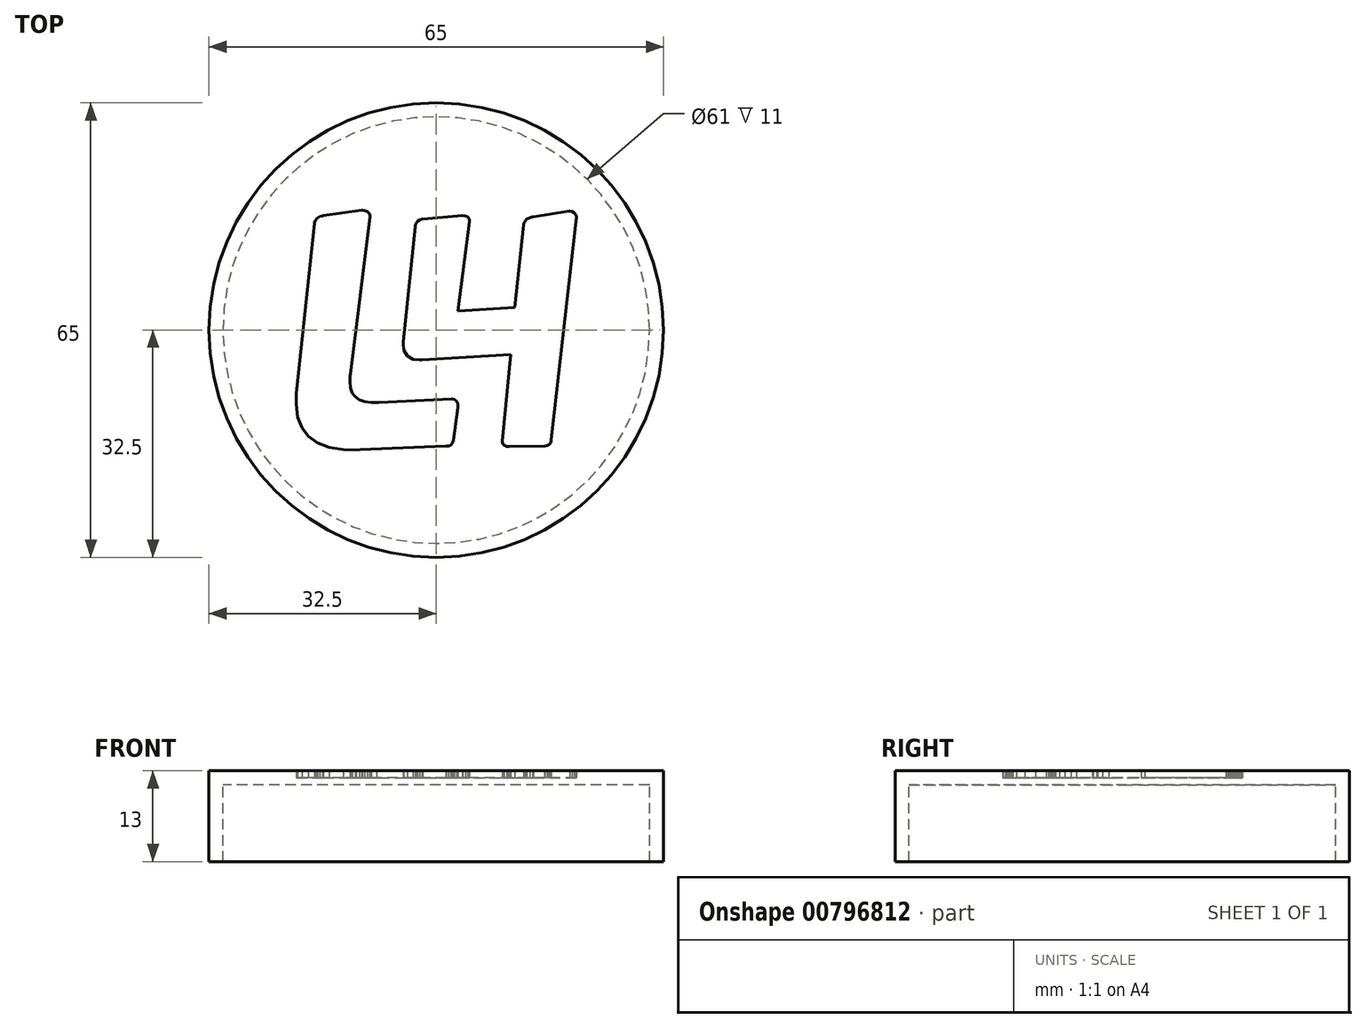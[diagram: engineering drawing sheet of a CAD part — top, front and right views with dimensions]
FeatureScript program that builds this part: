
annotation { "Feature Type Name" : "Feature", "Feature Type Description" : "" }
export const myFeature = defineFeature(function(context is Context, id is Id, definition is map)
    precondition{}
    {
        {
            var Q0;
            Q0=qCreatedBy(makeId("Top.planeOp"),FACE);
            var sketch = newSketch(context, id + "F0", { "sketchPlane" : qUnion([Q0])});
            skCircle(sketch, "E0", {"center": v(0, 0) * mm, "radius": 32.5 * mm});
            skSolve(sketch);
        }
        {
            var Q0;
            Q0 = qSketchRegion(id + "F0", true);
            extrude(context, id + "F1", {"entities" : qUnion([Q0]), "depth" : 2 * mm, "offsetDistance" : 25 * mm});
        }
        {
            var Q0;
            Q0=qCreatedBy(makeId("Top.planeOp"),FACE);
            var sketch = newSketch(context, id + "F2", { "sketchPlane" : qUnion([Q0])});
            skCircle(sketch, "E1.0", {"center": v(0, 0) * mm, "radius": 32.5 * mm});
            skCircle(sketch, "E2", {"center": v(0, 0) * mm, "radius": 30.5 * mm});
            skSolve(sketch);
        }
        {
            var Q0;
            Q0 = qSketchRegion(id + "F2", true);
            extrude(context, id + "F3", {"entities" : qUnion([Q0]), "operationType" : NewBodyOperationType.ADD, "oppositeDirection" : true, "depth" : 11 * mm, "offsetDistance" : 25 * mm});
        }
        {
            var Q0;
            Q0=qCreatedBy(makeId("Top.planeOp"),FACE);
            var sketch = newSketch(context, id + "F4", { "sketchPlane" : qUnion([Q0])});
            skLineSegment(sketch, "E3", {"start": v(2.44, -15.74) * mm, "end": v(2.42, -15.85) * mm});
            skLineSegment(sketch, "E4", {"start": v(2.42, -15.85) * mm, "end": v(2.32, -16.15) * mm});
            skLineSegment(sketch, "E5", {"start": v(2.32, -16.15) * mm, "end": v(2.1, -16.42) * mm});
            skLineSegment(sketch, "E6", {"start": v(2.1, -16.42) * mm, "end": v(1.79, -16.56) * mm});
            skLineSegment(sketch, "E7", {"start": v(1.79, -16.56) * mm, "end": v(1.48, -16.6) * mm});
            skLineSegment(sketch, "E8", {"start": v(1.48, -16.6) * mm, "end": v(1.38, -16.6) * mm});
            skLineSegment(sketch, "E9", {"start": v(1.38, -16.6) * mm, "end": v(-10.86, -17.1) * mm});
            skLineSegment(sketch, "E10", {"start": v(-10.86, -17.1) * mm, "end": v(-11.46, -17.13) * mm});
            skLineSegment(sketch, "E11", {"start": v(-11.46, -17.13) * mm, "end": v(-13.3, -17.07) * mm});
            skLineSegment(sketch, "E12", {"start": v(-13.3, -17.07) * mm, "end": v(-15.33, -16.74) * mm});
            skLineSegment(sketch, "E13", {"start": v(-15.33, -16.74) * mm, "end": v(-17, -16.1) * mm});
            skLineSegment(sketch, "E14", {"start": v(-17, -16.1) * mm, "end": v(-18.29, -15.17) * mm});
            skLineSegment(sketch, "E15", {"start": v(-18.29, -15.17) * mm, "end": v(-19.22, -13.94) * mm});
            skLineSegment(sketch, "E16", {"start": v(-19.22, -13.94) * mm, "end": v(-19.8, -12.42) * mm});
            skLineSegment(sketch, "E17", {"start": v(-19.8, -12.42) * mm, "end": v(-20.04, -10.59) * mm});
            skLineSegment(sketch, "E18", {"start": v(-20.04, -10.59) * mm, "end": v(-20.01, -9) * mm});
            skLineSegment(sketch, "E19", {"start": v(-20.01, -9) * mm, "end": v(-19.96, -8.46) * mm});
            skLineSegment(sketch, "E20", {"start": v(-19.96, -8.46) * mm, "end": v(-17.43, 15.25) * mm});
            skLineSegment(sketch, "E21", {"start": v(-17.43, 15.25) * mm, "end": v(-17.42, 15.35) * mm});
            skLineSegment(sketch, "E22", {"start": v(-17.42, 15.35) * mm, "end": v(-17.3, 15.66) * mm});
            skLineSegment(sketch, "E23", {"start": v(-17.3, 15.66) * mm, "end": v(-17.02, 16) * mm});
            skLineSegment(sketch, "E24", {"start": v(-17.02, 16) * mm, "end": v(-16.63, 16.23) * mm});
            skLineSegment(sketch, "E25", {"start": v(-16.63, 16.23) * mm, "end": v(-16.28, 16.34) * mm});
            skLineSegment(sketch, "E26", {"start": v(-16.28, 16.34) * mm, "end": v(-16.16, 16.36) * mm});
            skLineSegment(sketch, "E27", {"start": v(-16.16, 16.36) * mm, "end": v(-10.65, 17.12) * mm});
            skLineSegment(sketch, "E28", {"start": v(-10.65, 17.12) * mm, "end": v(-10.55, 17.13) * mm});
            skLineSegment(sketch, "E29", {"start": v(-10.55, 17.13) * mm, "end": v(-10.2, 17.1) * mm});
            skLineSegment(sketch, "E30", {"start": v(-10.2, 17.1) * mm, "end": v(-9.83, 16.93) * mm});
            skLineSegment(sketch, "E31", {"start": v(-9.83, 16.93) * mm, "end": v(-9.57, 16.62) * mm});
            skLineSegment(sketch, "E32", {"start": v(-9.57, 16.62) * mm, "end": v(-9.48, 16.3) * mm});
            skLineSegment(sketch, "E33", {"start": v(-9.48, 16.3) * mm, "end": v(-9.5, 16.2) * mm});
            skLineSegment(sketch, "E34", {"start": v(-9.5, 16.2) * mm, "end": v(-12.27, -6.3) * mm});
            skLineSegment(sketch, "E35", {"start": v(-12.27, -6.3) * mm, "end": v(-12.3, -6.56) * mm});
            skLineSegment(sketch, "E36", {"start": v(-12.3, -6.56) * mm, "end": v(-12.34, -7.37) * mm});
            skLineSegment(sketch, "E37", {"start": v(-12.34, -7.37) * mm, "end": v(-12.24, -8.27) * mm});
            skLineSegment(sketch, "E38", {"start": v(-12.24, -8.27) * mm, "end": v(-11.98, -8.99) * mm});
            skLineSegment(sketch, "E39", {"start": v(-11.98, -8.99) * mm, "end": v(-11.56, -9.54) * mm});
            skLineSegment(sketch, "E40", {"start": v(-11.56, -9.54) * mm, "end": v(-10.97, -9.95) * mm});
            skLineSegment(sketch, "E41", {"start": v(-10.97, -9.95) * mm, "end": v(-10.22, -10.2) * mm});
            skLineSegment(sketch, "E42", {"start": v(-10.22, -10.2) * mm, "end": v(-9.3, -10.33) * mm});
            skLineSegment(sketch, "E43", {"start": v(-9.3, -10.33) * mm, "end": v(-8.5, -10.35) * mm});
            skLineSegment(sketch, "E44", {"start": v(-8.5, -10.35) * mm, "end": v(-8.23, -10.33) * mm});
            skLineSegment(sketch, "E45", {"start": v(-8.23, -10.33) * mm, "end": v(2.19, -9.83) * mm});
            skLineSegment(sketch, "E46", {"start": v(2.19, -9.83) * mm, "end": v(2.3, -9.82) * mm});
            skLineSegment(sketch, "E47", {"start": v(2.3, -9.82) * mm, "end": v(2.62, -9.9) * mm});
            skLineSegment(sketch, "E48", {"start": v(2.62, -9.9) * mm, "end": v(2.93, -10.15) * mm});
            skLineSegment(sketch, "E49", {"start": v(2.93, -10.15) * mm, "end": v(3.09, -10.55) * mm});
            skLineSegment(sketch, "E50", {"start": v(3.09, -10.55) * mm, "end": v(3.11, -10.92) * mm});
            skLineSegment(sketch, "E51", {"start": v(3.11, -10.92) * mm, "end": v(3.1, -11.04) * mm});
            skLineSegment(sketch, "E52", {"start": v(3.1, -11.04) * mm, "end": v(2.44, -15.74) * mm});
            skLineSegment(sketch, "E53", {"start": v(-3.02, 14.8) * mm, "end": v(-3.01, 14.9) * mm});
            skLineSegment(sketch, "E54", {"start": v(-3.01, 14.9) * mm, "end": v(-2.92, 15.2) * mm});
            skLineSegment(sketch, "E55", {"start": v(-2.92, 15.2) * mm, "end": v(-2.71, 15.53) * mm});
            skLineSegment(sketch, "E56", {"start": v(-2.71, 15.53) * mm, "end": v(-2.37, 15.75) * mm});
            skLineSegment(sketch, "E57", {"start": v(-2.37, 15.75) * mm, "end": v(-2.03, 15.84) * mm});
            skLineSegment(sketch, "E58", {"start": v(-2.03, 15.84) * mm, "end": v(-1.9, 15.85) * mm});
            skLineSegment(sketch, "E59", {"start": v(-1.9, 15.85) * mm, "end": v(3.7, 16.36) * mm});
            skLineSegment(sketch, "E60", {"start": v(3.7, 16.36) * mm, "end": v(3.82, 16.37) * mm});
            skLineSegment(sketch, "E61", {"start": v(3.82, 16.37) * mm, "end": v(4.16, 16.33) * mm});
            skLineSegment(sketch, "E62", {"start": v(4.16, 16.33) * mm, "end": v(4.52, 16.18) * mm});
            skLineSegment(sketch, "E63", {"start": v(4.52, 16.18) * mm, "end": v(4.73, 15.9) * mm});
            skLineSegment(sketch, "E64", {"start": v(4.73, 15.9) * mm, "end": v(4.78, 15.6) * mm});
            skLineSegment(sketch, "E65", {"start": v(4.78, 15.6) * mm, "end": v(4.77, 15.5) * mm});
            skLineSegment(sketch, "E66", {"start": v(4.77, 15.5) * mm, "end": v(3.1, 2.7) * mm});
            skLineSegment(sketch, "E67", {"start": v(3.1, 2.7) * mm, "end": v(11.24, 3.21) * mm});
            skLineSegment(sketch, "E68", {"start": v(11.24, 3.21) * mm, "end": v(12.5, 15.04) * mm});
            skLineSegment(sketch, "E69", {"start": v(12.5, 15.04) * mm, "end": v(12.52, 15.17) * mm});
            skLineSegment(sketch, "E70", {"start": v(12.52, 15.17) * mm, "end": v(12.66, 15.53) * mm});
            skLineSegment(sketch, "E71", {"start": v(12.66, 15.53) * mm, "end": v(12.96, 15.87) * mm});
            skLineSegment(sketch, "E72", {"start": v(12.96, 15.87) * mm, "end": v(13.39, 16.09) * mm});
            skLineSegment(sketch, "E73", {"start": v(13.39, 16.09) * mm, "end": v(13.78, 16.19) * mm});
            skLineSegment(sketch, "E74", {"start": v(13.78, 16.19) * mm, "end": v(13.92, 16.2) * mm});
            skLineSegment(sketch, "E75", {"start": v(13.92, 16.2) * mm, "end": v(18.97, 17.02) * mm});
            skLineSegment(sketch, "E76", {"start": v(18.97, 17.02) * mm, "end": v(19.08, 17.03) * mm});
            skLineSegment(sketch, "E77", {"start": v(19.08, 17.03) * mm, "end": v(19.42, 16.99) * mm});
            skLineSegment(sketch, "E78", {"start": v(19.42, 16.99) * mm, "end": v(19.77, 16.79) * mm});
            skLineSegment(sketch, "E79", {"start": v(19.77, 16.79) * mm, "end": v(19.98, 16.48) * mm});
            skLineSegment(sketch, "E80", {"start": v(19.98, 16.48) * mm, "end": v(20.04, 16.2) * mm});
            skLineSegment(sketch, "E81", {"start": v(20.04, 16.2) * mm, "end": v(20.03, 16.1) * mm});
            skLineSegment(sketch, "E82", {"start": v(20.03, 16.1) * mm, "end": v(16.44, -15.7) * mm});
            skLineSegment(sketch, "E83", {"start": v(16.44, -15.7) * mm, "end": v(16.44, -15.8) * mm});
            skLineSegment(sketch, "E84", {"start": v(16.44, -15.8) * mm, "end": v(16.34, -16.1) * mm});
            skLineSegment(sketch, "E85", {"start": v(16.34, -16.1) * mm, "end": v(16.13, -16.37) * mm});
            skLineSegment(sketch, "E86", {"start": v(16.13, -16.37) * mm, "end": v(15.84, -16.51) * mm});
            skLineSegment(sketch, "E87", {"start": v(15.84, -16.51) * mm, "end": v(15.57, -16.55) * mm});
            skLineSegment(sketch, "E88", {"start": v(15.57, -16.55) * mm, "end": v(15.48, -16.55) * mm});
            skLineSegment(sketch, "E89", {"start": v(15.48, -16.55) * mm, "end": v(10.48, -16.65) * mm});
            skLineSegment(sketch, "E90", {"start": v(10.48, -16.65) * mm, "end": v(10.37, -16.65) * mm});
            skLineSegment(sketch, "E91", {"start": v(10.37, -16.65) * mm, "end": v(10.06, -16.61) * mm});
            skLineSegment(sketch, "E92", {"start": v(10.06, -16.61) * mm, "end": v(9.73, -16.48) * mm});
            skLineSegment(sketch, "E93", {"start": v(9.73, -16.48) * mm, "end": v(9.52, -16.23) * mm});
            skLineSegment(sketch, "E94", {"start": v(9.52, -16.23) * mm, "end": v(9.46, -15.94) * mm});
            skLineSegment(sketch, "E95", {"start": v(9.46, -15.94) * mm, "end": v(9.47, -15.84) * mm});
            skLineSegment(sketch, "E96", {"start": v(9.47, -15.84) * mm, "end": v(10.68, -3.5) * mm});
            skLineSegment(sketch, "E97", {"start": v(10.68, -3.5) * mm, "end": v(-2.06, -4.27) * mm});
            skLineSegment(sketch, "E98", {"start": v(-2.06, -4.27) * mm, "end": v(-2.36, -4.28) * mm});
            skLineSegment(sketch, "E99", {"start": v(-2.36, -4.28) * mm, "end": v(-3.29, -4.16) * mm});
            skLineSegment(sketch, "E100", {"start": v(-3.29, -4.16) * mm, "end": v(-4.15, -3.7) * mm});
            skLineSegment(sketch, "E101", {"start": v(-4.15, -3.7) * mm, "end": v(-4.63, -2.85) * mm});
            skLineSegment(sketch, "E102", {"start": v(-4.63, -2.85) * mm, "end": v(-4.72, -1.94) * mm});
            skLineSegment(sketch, "E103", {"start": v(-4.72, -1.94) * mm, "end": v(-4.69, -1.64) * mm});
            skLineSegment(sketch, "E104", {"start": v(-4.69, -1.64) * mm, "end": v(-3.02, 14.8) * mm});
            skSolve(sketch);
        }
        {
            var Q0;
            Q0 = qSketchRegion(id + "F4", true);
            extrude(context, id + "F5", {"entities" : qUnion([Q0]), "operationType" : NewBodyOperationType.REMOVE, "surfaceOperationType" : NewSurfaceOperationType.ADD, "depth" : 3 * mm, "offsetDistance" : 25 * mm, "hasSecondDirection" : true, "secondDirectionOppositeDirection" : false, "secondDirectionDepth" : 1 * mm});
        }
    });
